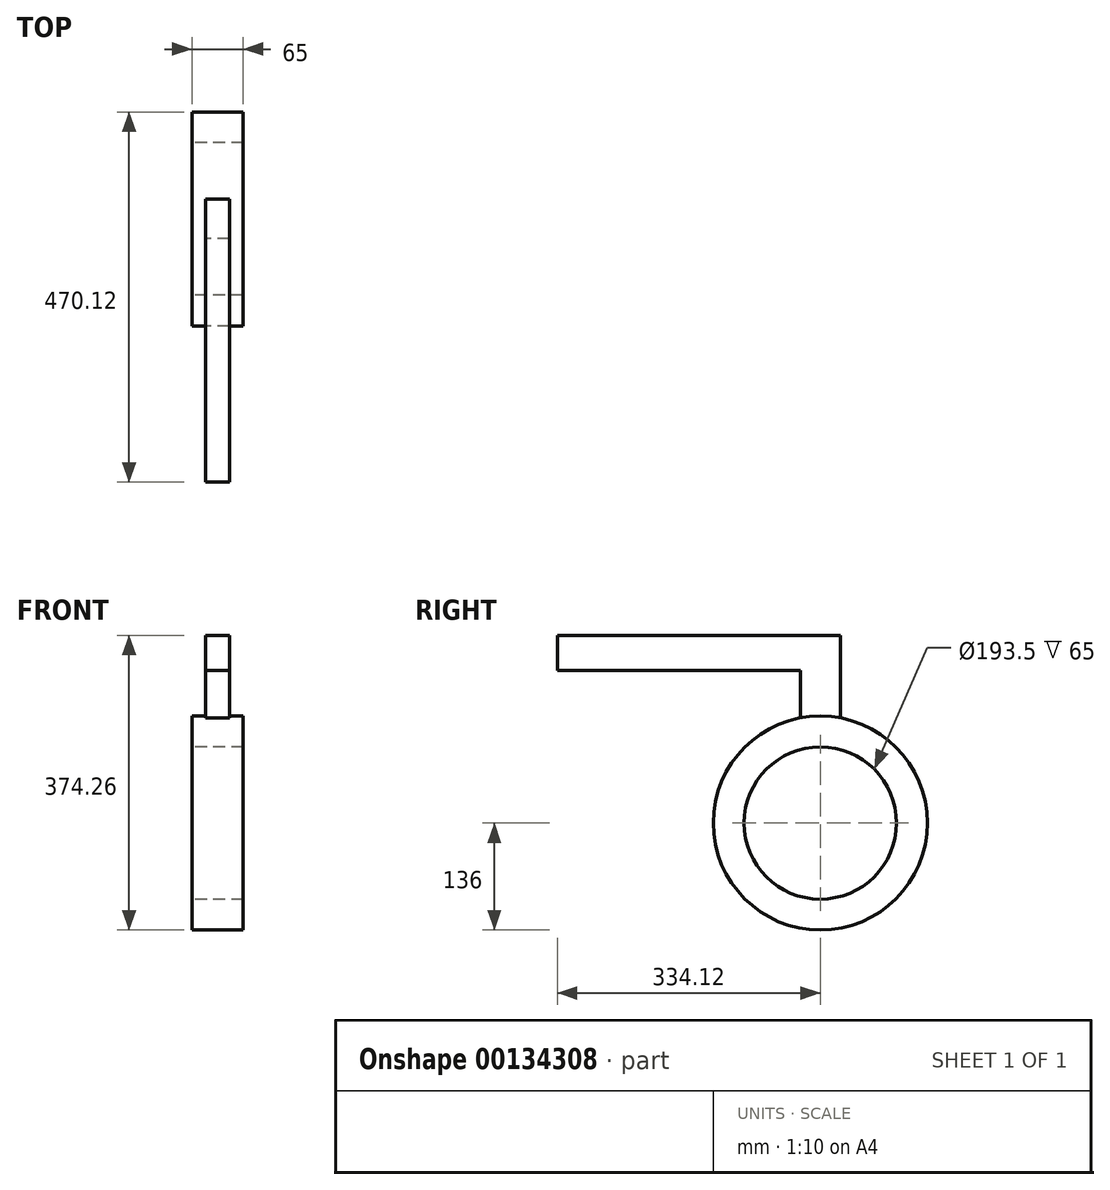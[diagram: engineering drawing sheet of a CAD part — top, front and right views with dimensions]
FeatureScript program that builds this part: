
annotation { "Feature Type Name" : "Feature", "Feature Type Description" : "" }
export const myFeature = defineFeature(function(context is Context, id is Id, definition is map)
    precondition{}
    {
        {
            var Q0;
            Q0=qCreatedBy(makeId("Front.planeOp"),FACE);
            var sketch = newSketch(context, id + "F0", { "sketchPlane" : qUnion([Q0])});
            skLineSegment(sketch, "E0.bottom", {"start": v(-32.5, 136) * mm, "end": v(32.5, 136) * mm});
            skLineSegment(sketch, "E0.top", {"start": v(-32.5, 96.75) * mm, "end": v(32.5, 96.75) * mm});
            skLineSegment(sketch, "E0.left", {"start": v(-32.5, 136) * mm, "end": v(-32.5, 96.75) * mm});
            skLineSegment(sketch, "E0.right", {"start": v(32.5, 136) * mm, "end": v(32.5, 96.75) * mm});
            skLineSegment(sketch, "E1", {"start": v(24.95, 0) * mm, "end": v(70.4, 0) * mm, "construction": true});
            skSolve(sketch);
        }
        {
            var Q0;
            Q0=makeQuery(id+"F0.imprint","IMPRINT",FACE,{"disambiguationData":[TD([[makeQuery(id+"F0.imprint","IMPRINT",EDGE,{"derivedFrom":sQuery(id+"F0.wireOp",EDGE,"E0.bottom")}),-1.0]])]});
            var Q1;
            Q1=sQuery(id+"F0.wireOp",EDGE,"E1");
            revolve(context, id + "F1", {"entities" : qUnion([Q0]), "axis" : qUnion([Q1]), "revolveType" : RevolveType.FULL});
        }
        {
            var Q0;
            Q0=qCreatedBy(makeId("Right.planeOp"),FACE);
            var sketch = newSketch(context, id + "F2", { "sketchPlane" : qUnion([Q0])});
            skLineSegment(sketch, "E2", {"start": v(25.21, 112.72) * mm, "end": v(25.21, 238.26) * mm});
            skLineSegment(sketch, "E3", {"start": v(25.21, 238.26) * mm, "end": v(-334.12, 238.26) * mm});
            skLineSegment(sketch, "E4", {"start": v(-334.12, 238.26) * mm, "end": v(-334.12, 193.83) * mm});
            skLineSegment(sketch, "E5", {"start": v(-334.12, 193.83) * mm, "end": v(-25.21, 193.83) * mm});
            skLineSegment(sketch, "E6", {"start": v(-25.21, 193.83) * mm, "end": v(-25.21, 112.72) * mm});
            skLineSegment(sketch, "E7", {"start": v(25.21, 112.72) * mm, "end": v(-25.21, 112.72) * mm});
            skSolve(sketch);
        }
        {
            var Q0;
            Q0=makeQuery(id+"F2.imprint","IMPRINT",FACE,{"disambiguationData":[TD([[makeQuery(id+"F2.imprint","IMPRINT",EDGE,{"derivedFrom":sQuery(id+"F2.wireOp",EDGE,"E2")}),1.0]])]});
            extrude(context, id + "F3", {"entities" : qUnion([Q0]), "operationType" : NewBodyOperationType.ADD, "endBound" : BoundingType.SYMMETRIC, "depth" : 30 * mm});
        }
    });
